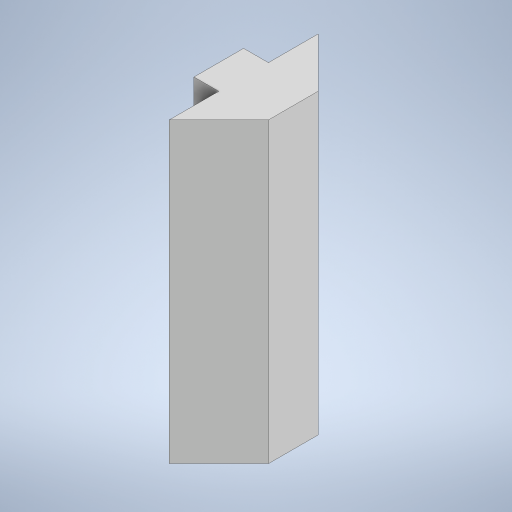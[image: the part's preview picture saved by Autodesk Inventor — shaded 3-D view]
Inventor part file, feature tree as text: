
AUTODESK INVENTOR PART (.ipt)
format: ipt  version: 2023 (Build 270158000, 158)  size: 217,600 bytes
history: native  units: mm
features: other x1, extrude x1, sketch x1
ambient origin geometry x8: Origin, YZ Plane, XZ Plane, XY Plane, X Axis, Y Axis, Z Axis, Center Point
bodies: Body1 (feature_tree)
feature tree (3):
  other  "Твердое тело1"
  extrude  "Выдавливание1"  Depth=10.0mm
  sketch  "Эскиз1"
